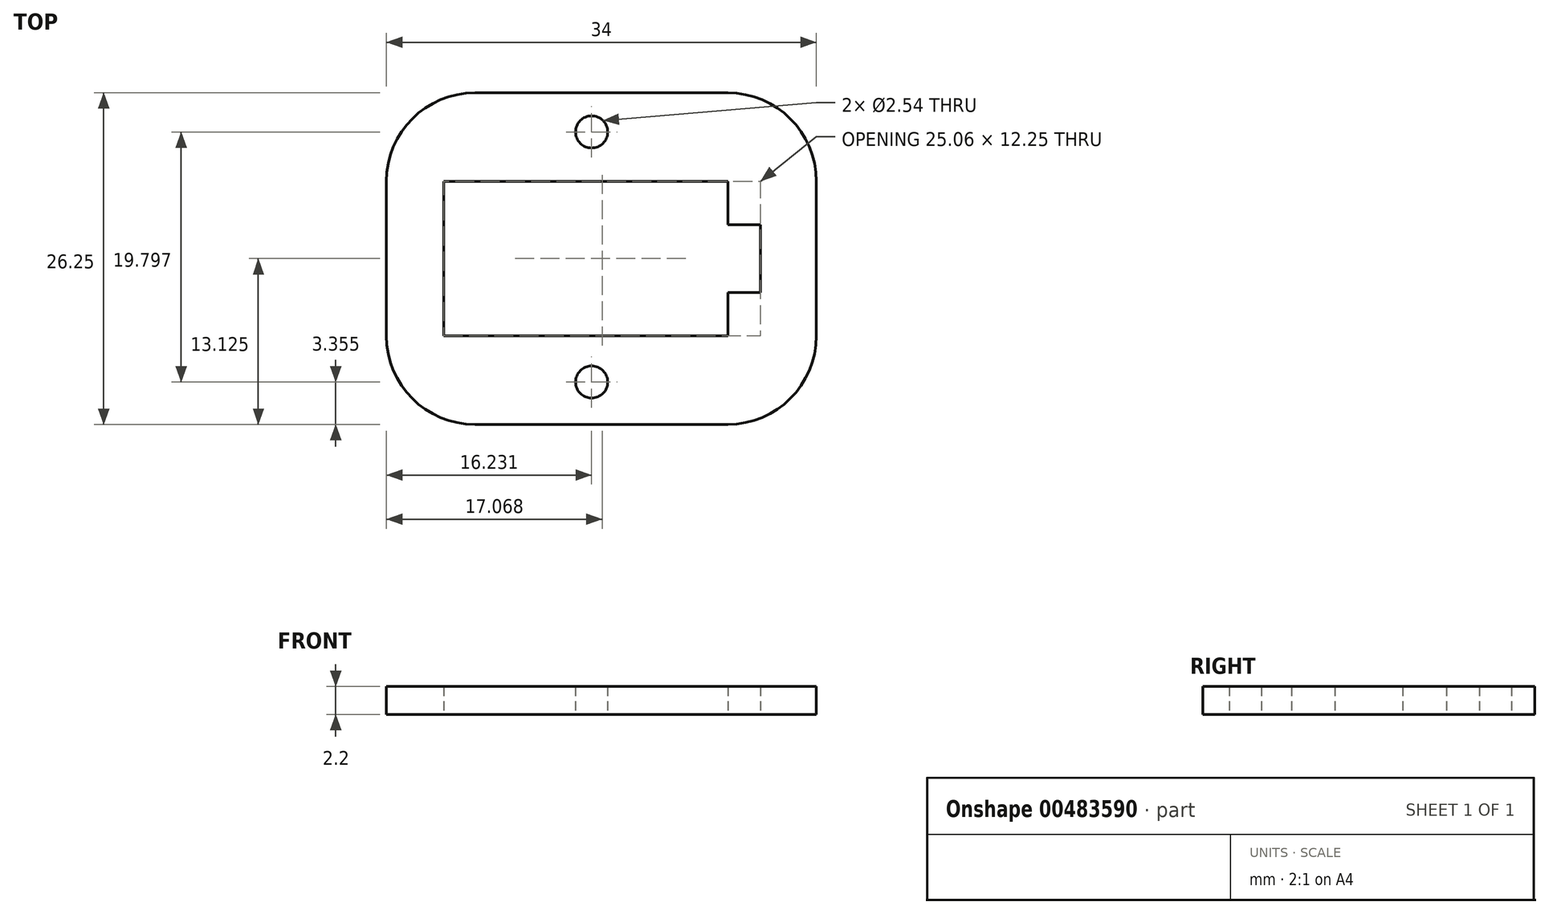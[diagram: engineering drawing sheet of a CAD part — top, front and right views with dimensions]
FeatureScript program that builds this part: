
annotation { "Feature Type Name" : "Feature", "Feature Type Description" : "" }
export const myFeature = defineFeature(function(context is Context, id is Id, definition is map)
    precondition{}
    {
        {
            var Q0;
            Q0=qCreatedBy(makeId("Top.planeOp"),FACE);
            var sketch = newSketch(context, id + "F0", { "sketchPlane" : qUnion([Q0])});
            skLineSegment(sketch, "E0.bottom", {"start": v(7, 0) * mm, "end": v(27, 0) * mm});
            skLineSegment(sketch, "E0.top", {"start": v(7, 26.25) * mm, "end": v(27, 26.25) * mm});
            skLineSegment(sketch, "E0.left", {"start": v(0, 7) * mm, "end": v(0, 19.25) * mm});
            skLineSegment(sketch, "E0.right", {"start": v(34, 7) * mm, "end": v(34, 19.25) * mm});
            skPoint(sketch, "E1.visualSharp", {"position": v(0, 26.25) * mm});
            skArc(sketch, "E1.filletArc", {"start": v(7, 26.25) * mm, "mid": v(2.05, 24.2) * mm, "end": v(0, 19.25) * mm});
            skPoint(sketch, "E2.visualSharp", {"position": v(0, 0) * mm});
            skArc(sketch, "E2.filletArc", {"start": v(0, 7) * mm, "mid": v(2.05, 2.05) * mm, "end": v(7, 0) * mm});
            skPoint(sketch, "E3.visualSharp", {"position": v(34, 0) * mm});
            skArc(sketch, "E3.filletArc", {"start": v(27, 0) * mm, "mid": v(31.95, 2.05) * mm, "end": v(34, 7) * mm});
            skPoint(sketch, "E4.visualSharp", {"position": v(34, 26.25) * mm});
            skArc(sketch, "E4.filletArc", {"start": v(34, 19.25) * mm, "mid": v(31.95, 24.2) * mm, "end": v(27, 26.25) * mm});
            skLineSegment(sketch, "E5", {"start": v(4.54, 19.25) * mm, "end": v(27, 19.25) * mm});
            skLineSegment(sketch, "E6", {"start": v(4.54, 19.25) * mm, "end": v(4.54, 7) * mm});
            skLineSegment(sketch, "E7", {"start": v(4.54, 7) * mm, "end": v(27, 7) * mm});
            skLineSegment(sketch, "E8", {"start": v(27, 19.25) * mm, "end": v(27, 15.8) * mm});
            skLineSegment(sketch, "E9", {"start": v(27, 7) * mm, "end": v(27, 10.45) * mm});
            skCircle(sketch, "E10", {"center": v(16.23, 23.15) * mm, "radius": 1.27 * mm});
            skCircle(sketch, "E11", {"center": v(16.23, 3.36) * mm, "radius": 1.27 * mm});
            skLineSegment(sketch, "E12", {"start": v(27, 15.8) * mm, "end": v(29.6, 15.8) * mm});
            skLineSegment(sketch, "E13", {"start": v(29.6, 15.8) * mm, "end": v(29.6, 10.45) * mm});
            skLineSegment(sketch, "E14", {"start": v(29.6, 10.45) * mm, "end": v(27, 10.45) * mm});
            skLineSegment(sketch, "E15.trimOffspring", {"start": v(27, 10.45) * mm, "end": v(27, 7) * mm});
            skSolve(sketch);
        }
        {
            var Q0;
            Q0=makeQuery(id+"F0.imprint","IMPRINT",FACE,{"disambiguationData":[TD([[makeQuery(id+"F0.imprint","IMPRINT",EDGE,{"derivedFrom":sQuery(id+"F0.wireOp",EDGE,"E0.bottom")}),1.0]])]});
            extrude(context, id + "F1", {"entities" : qUnion([Q0]), "depth" : 2.2 * mm});
        }
    });
